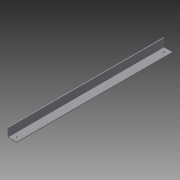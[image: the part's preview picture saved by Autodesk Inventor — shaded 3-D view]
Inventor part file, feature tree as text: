
AUTODESK INVENTOR PART (.ipt)
format: ipt  version: 2015 (Build 190159000, 159)  size: 113,664 bytes
history: native  units: in
note: dims shown in document units (in); Inventor stores cm internally (conversion verified against a paired STEP export)
features: extrude x2
ambient origin geometry x8: Origin, YZ Plane, XZ Plane, XY Plane, X Axis, Y Axis, Z Axis, Center Point
bodies: Body1 (feature_tree)
feature tree (2):
  extrude  "Extrusion4"  Depth=25.5906in
  extrude  "Extrusion5"  Depth=25.5906in
